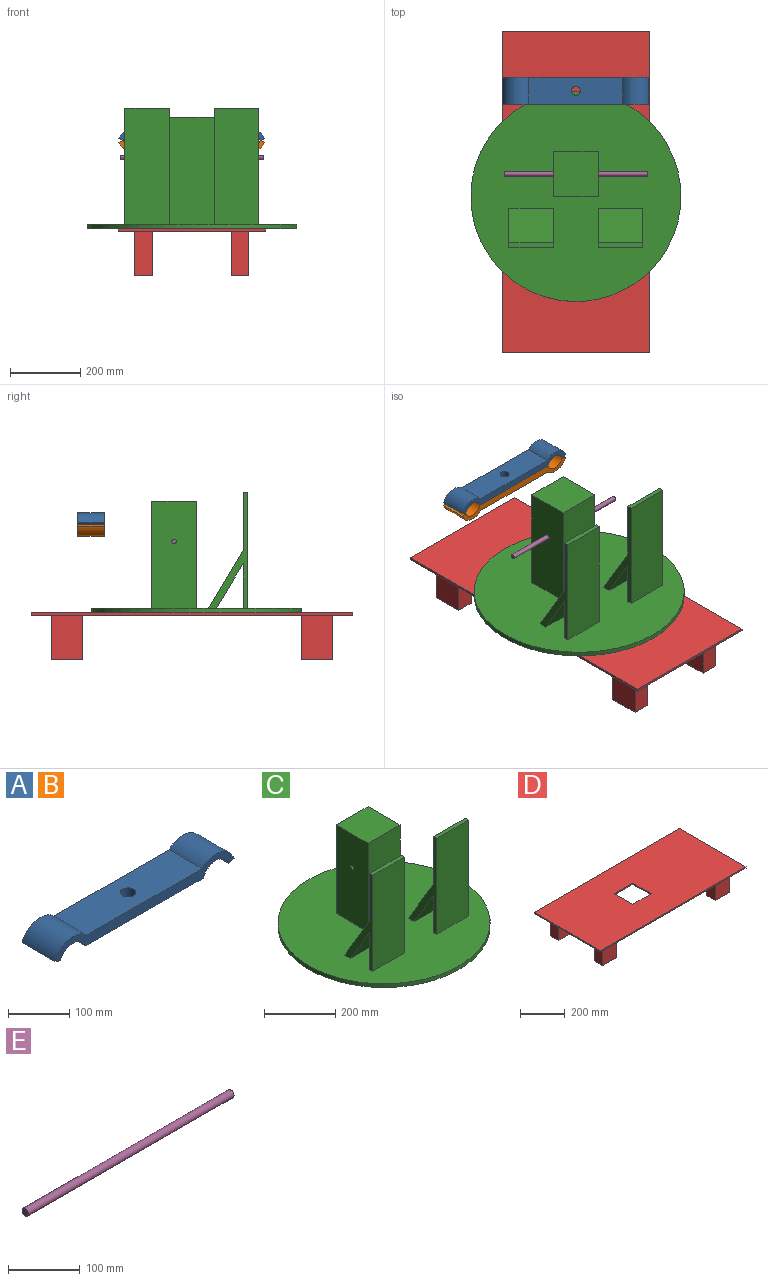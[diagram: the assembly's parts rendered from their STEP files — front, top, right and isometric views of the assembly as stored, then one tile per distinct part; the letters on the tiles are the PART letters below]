
ASSEMBLY  parts=5 mates=3
PART A: 11 faces, bbox 414.2x76.2x33.7 mm
  f0: plane 270.8x76.2mm, normal (0,0,-1), area 20128.3mm2, adj f1,f7,f8,f9,f10
  f1: cylinder r=31.75mm len=76.2mm, axis (0,1,0), area 5852.1mm2, adj f0,f2,f8,f9
  f2: plane 76.2x12.3mm, normal (0.35,0,-0.94), area 1002.1mm2, adj f1,f3,f8,f9
  f3: cylinder r=44.9mm len=76.2mm, axis (0,1,0), area 6825.3mm2, adj f2,f4,f8,f9
  f4: plane 266.7x76.2mm, normal (0,0,1), area 19815.8mm2, adj f3,f5,f8,f9,f10
  f5: cylinder r=44.9mm len=76.2mm, axis (0,1,0), area 6825.3mm2, adj f4,f6,f8,f9
  f6: plane 76.2x12.3mm, normal (-0.35,0,-0.94), area 1002.1mm2, adj f5,f7,f8,f9
  f7: cylinder r=31.75mm len=76.2mm, axis (0,1,0), area 5852.1mm2, adj f0,f6,f8,f9
  f8: plane 414.2x33.68mm, normal (0,-1,0), area 7686mm2, adj f0,f1,f2,f3,f4,f5,f6,f7
  f9: plane 414.2x33.68mm, normal (0,1,0), area 7686mm2, adj f0,f1,f2,f3,f4,f5,f6,f7
  f10: cylinder r=12.7mm len=25.4mm, axis (0,0,1), area 1637.8mm2, adj f0,f4
PART B: same geometry as A
PART C: 31 faces, bbox 596.9x596.9x342.9 mm
  f0: plane 127x126.61mm, normal (0,1,0), area 16079.2mm2, adj f1,f17,f19,f29
  f1: plane 596.9x596.9mm, normal (0,0,1), area 254611.9mm2, adj f0,f2,f3,f4,f5,f6,f15,f17
  f2: plane 127x126.61mm, normal (0,1,0), area 16079.1mm2, adj f1,f22,f24,f27
  f3: plane 304.8x127mm, normal (-1,0,0), area 38582.9mm2, adj f1,f4,f6,f7,f14
  f4: plane 304.8x127mm, normal (0,-1,0), area 38709.6mm2, adj f1,f3,f5,f7
  f5: plane 304.8x127mm, normal (1,0,0), area 38582.9mm2, adj f1,f4,f6,f7,f13
  f6: plane 304.8x127mm, normal (0,1,0), area 38709.6mm2, adj f1,f3,f5,f7
  f7: plane 127x127mm, normal (0,0,1), area 16129mm2, adj f3,f4,f5,f6
  f8: plane 304.8x101.6mm, normal (1,0,0), area 30841mm2, adj f9,f11,f12,f14,f16
  f9: plane 304.8x101.6mm, normal (0,-1,0), area 30967.7mm2, adj f8,f10,f12,f16
  f10: plane 304.8x101.6mm, normal (-1,0,0), area 30841mm2, adj f9,f11,f12,f13,f16
  f11: plane 304.8x101.6mm, normal (0,1,0), area 30967.7mm2, adj f8,f10,f12,f16
  f12: plane 101.6x101.6mm, normal (0,0,-1), area 10322.6mm2, adj f8,f9,f10,f11
  f13: cylinder r=6.35mm len=12.7mm, axis (-1,0,0), area 506.7mm2, adj f5,f10
  f14: cylinder r=6.35mm len=12.7mm, axis (-1,0,0), area 506.7mm2, adj f3,f8
  f15: cylinder r=298.45mm len=596.9mm, axis (0,0,1), area 23815.3mm2, adj f1,f16
  f16: plane 596.9x596.9mm, normal (0,0,-1), area 269506.6mm2, adj f8,f9,f10,f11,f15
  f17: plane 330.2x111.7mm, normal (1,0,0), area 7559.9mm2, adj f0,f1,f18,f20,f21,f29,f30
  f18: plane 165.1x127mm, normal (0,1,0), area 20967.7mm2, adj f17,f19,f21,f30
  f19: plane 330.2x111.7mm, normal (-1,0,0), area 7559.9mm2, adj f0,f1,f18,f20,f21,f29,f30
  f20: plane 330.2x127mm, normal (0,-1,0), area 41935.4mm2, adj f1,f17,f19,f21
  f21: plane 127x12.7mm, normal (0,0,1), area 1612.9mm2, adj f17,f18,f19,f20
  f22: plane 330.2x111.7mm, normal (-1,0,0), area 7559.9mm2, adj f1,f2,f23,f25,f26,f27,f28
  f23: plane 330.2x127mm, normal (0,-1,0), area 41935.4mm2, adj f1,f22,f24,f26
  f24: plane 330.2x111.7mm, normal (1,0,0), area 7559.9mm2, adj f1,f2,f23,f25,f26,f27,f28
  f25: plane 165.1x127mm, normal (0,1,0), area 20967.7mm2, adj f22,f24,f26,f28
  f26: plane 127x12.7mm, normal (0,0,1), area 1612.9mm2, adj f22,f23,f24,f25
  f27: plane 127x126.61mm, normal (0,-0.86,-0.51), area 18748.1mm2, adj f1,f2,f22,f24
  f28: plane 165.1x127mm, normal (0,0.86,0.51), area 24448.1mm2, adj f1,f22,f24,f25
  f29: plane 127x126.61mm, normal (0,-0.86,-0.51), area 18748.1mm2, adj f0,f1,f17,f19
  f30: plane 165.1x127mm, normal (0,0.86,0.51), area 24448.2mm2, adj f1,f17,f18,f19
PART D: 30 faces, bbox 914.4x419.1x133.4 mm
  f0: plane 914.4x419.1mm, normal (0,0,-1), area 352096.1mm2, adj f2,f3,f4,f5,f6,f7,f8,f9
  f1: plane 914.4x419.1mm, normal (0,0,1), area 370160.5mm2, adj f2,f3,f4,f5,f26,f27,f28,f29
  f2: plane 419.1x6.35mm, normal (-1,0,0), area 2661.3mm2, adj f0,f1,f3,f5
  f3: plane 914.4x6.35mm, normal (0,-1,0), area 5806.4mm2, adj f0,f1,f2,f4
  f4: plane 419.1x6.35mm, normal (1,0,0), area 2661.3mm2, adj f0,f1,f3,f5
  f5: plane 914.4x6.35mm, normal (0,1,0), area 5806.4mm2, adj f0,f1,f2,f4
  f6: plane 127x50.8mm, normal (-1,0,0), area 6451.6mm2, adj f0,f7,f9,f10
  f7: plane 127x88.9mm, normal (0,1,0), area 11290.3mm2, adj f0,f6,f8,f10
  f8: plane 127x50.8mm, normal (1,0,0), area 6451.6mm2, adj f0,f7,f9,f10
  f9: plane 127x88.9mm, normal (0,-1,0), area 11290.3mm2, adj f0,f6,f8,f10
  f10: plane 88.9x50.8mm, normal (0,0,-1), area 4516.1mm2, adj f6,f7,f8,f9
  f11: plane 127x50.8mm, normal (-1,0,0), area 6451.6mm2, adj f0,f12,f14,f15
  f12: plane 127x88.9mm, normal (0,1,0), area 11290.3mm2, adj f0,f11,f13,f15
  f13: plane 127x50.8mm, normal (1,0,0), area 6451.6mm2, adj f0,f12,f14,f15
  f14: plane 127x88.9mm, normal (0,-1,0), area 11290.3mm2, adj f0,f11,f13,f15
  f15: plane 88.9x50.8mm, normal (0,0,-1), area 4516.1mm2, adj f11,f12,f13,f14
  f16: plane 127x88.9mm, normal (0,1,0), area 11290.3mm2, adj f0,f17,f19,f20
  f17: plane 127x50.8mm, normal (1,0,0), area 6451.6mm2, adj f0,f16,f18,f20
  f18: plane 127x88.9mm, normal (0,-1,0), area 11290.3mm2, adj f0,f17,f19,f20
  f19: plane 127x50.8mm, normal (-1,0,0), area 6451.6mm2, adj f0,f16,f18,f20
  f20: plane 88.9x50.8mm, normal (0,0,-1), area 4516.1mm2, adj f16,f17,f18,f19
  f21: plane 127x88.9mm, normal (0,1,0), area 11290.3mm2, adj f0,f22,f24,f25
  f22: plane 127x50.8mm, normal (1,0,0), area 6451.6mm2, adj f0,f21,f23,f25
  f23: plane 127x88.9mm, normal (0,-1,0), area 11290.3mm2, adj f0,f22,f24,f25
  f24: plane 127x50.8mm, normal (-1,0,0), area 6451.6mm2, adj f0,f21,f23,f25
  f25: plane 88.9x50.8mm, normal (0,0,-1), area 4516.1mm2, adj f21,f22,f23,f24
  f26: plane 114.3x6.35mm, normal (0,-1,0), area 725.8mm2, adj f0,f1,f27,f29
  f27: plane 114.3x6.35mm, normal (1,0,0), area 725.8mm2, adj f0,f1,f26,f28
  f28: plane 114.3x6.35mm, normal (0,1,0), area 725.8mm2, adj f0,f1,f27,f29
  f29: plane 114.3x6.35mm, normal (-1,0,0), area 725.8mm2, adj f0,f1,f26,f28
PART E: 3 faces, bbox 406.4x12.7x12.7 mm
  f0: cylinder r=6.35mm len=406.4mm, axis (1,0,0), area 16214.6mm2, adj f1,f2
  f1: plane 12.7x12.7mm, normal (-1,0,0), area 126.7mm2, adj f0
  f2: plane 12.7x12.7mm, normal (1,0,0), area 126.7mm2, adj f0
PLACE A t=(-430.32,207.13,261.07)mm
PLACE B rot(axis=(1,0,0),180deg) t=(-430.32,130.93,251.77)mm
PLACE C t=(-433.97,-64.34,18.1)mm
PLACE D rot(axis=(0,0,-1),90deg) t=(-267.65,-109.7,-0.95)mm
PLACE E t=(-227.03,-66.99,208.6)mm
MATE fastened D.f1 <-> C.f16  axis (0,0,1) through (-430.23,-16.19,5.4)mm
MATE fastened E.f0 <-> C.f13  axis (1,0,0) through (-430.23,-66.99,208.6)mm
MATE fastened B.f10 <-> A.f10  axis (0,0,1) through (-430.32,169.03,256.42)mm
